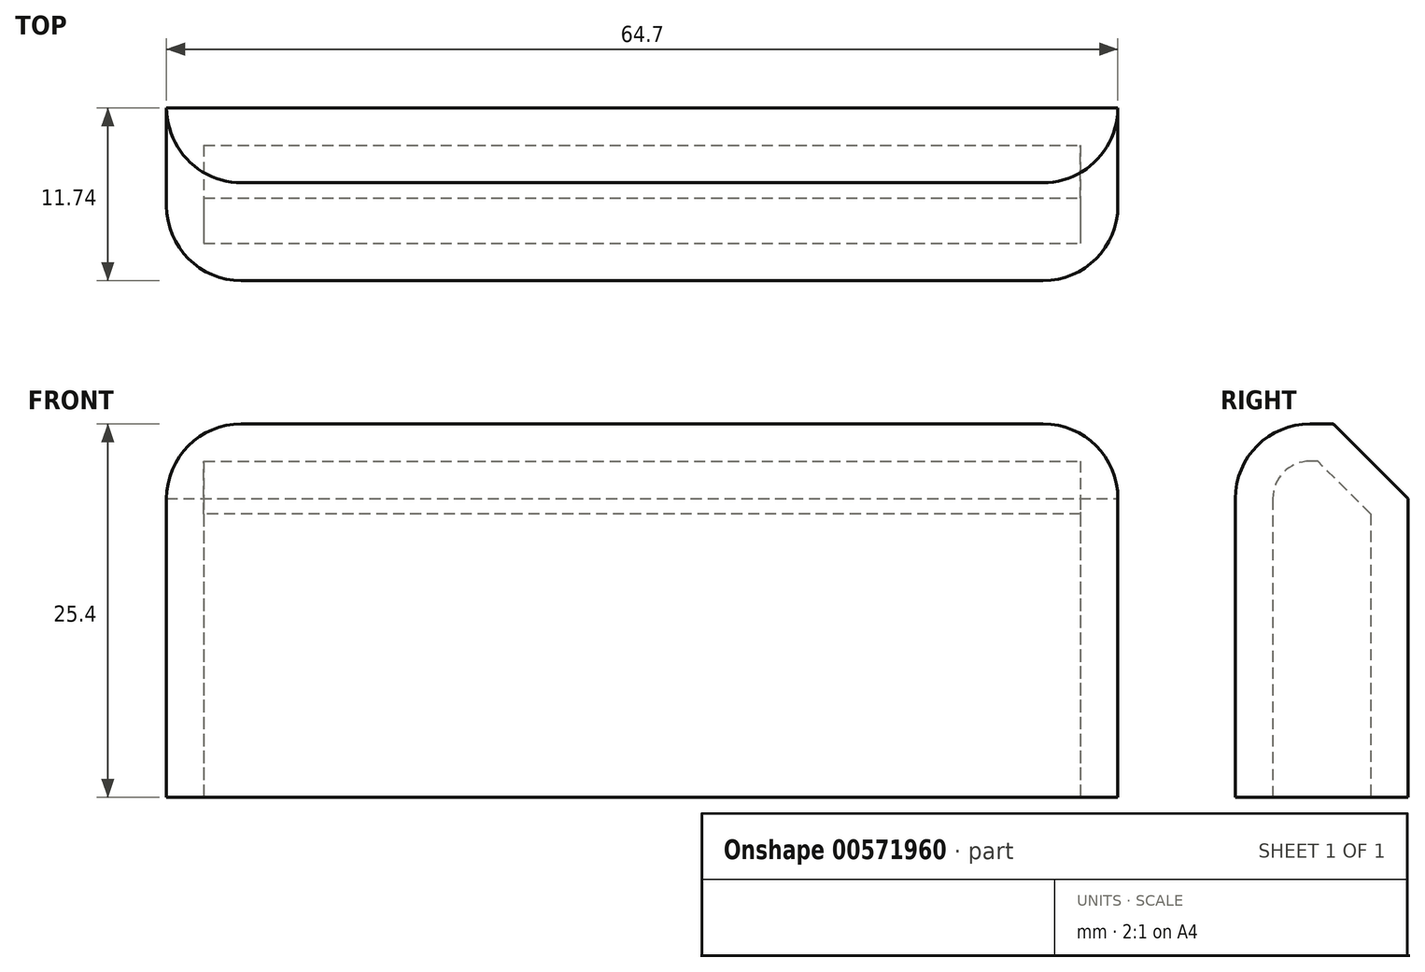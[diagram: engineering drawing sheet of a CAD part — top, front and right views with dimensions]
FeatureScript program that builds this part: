
annotation { "Feature Type Name" : "Feature", "Feature Type Description" : "" }
export const myFeature = defineFeature(function(context is Context, id is Id, definition is map)
    precondition{}
    {
        {
            var Q0;
            Q0=qCreatedBy(makeId("Top.planeOp"),FACE);
            var sketch = newSketch(context, id + "F0", { "sketchPlane" : qUnion([Q0])});
            skLineSegment(sketch, "E0.bottom", {"start": v(-24.66, 46.8) * mm, "end": v(40.04, 46.8) * mm});
            skLineSegment(sketch, "E0.top", {"start": v(-24.66, 35.06) * mm, "end": v(40.04, 35.06) * mm});
            skLineSegment(sketch, "E0.left", {"start": v(-24.66, 46.8) * mm, "end": v(-24.66, 35.06) * mm});
            skLineSegment(sketch, "E0.right", {"start": v(40.04, 46.8) * mm, "end": v(40.04, 35.06) * mm});
            skSolve(sketch);
        }
        {
            var Q0;
            Q0=makeQuery(id+"F0.imprint","IMPRINT",FACE,{"disambiguationData":[TD([[makeQuery(id+"F0.imprint","IMPRINT",EDGE,{"derivedFrom":sQuery(id+"F0.wireOp",EDGE,"E0.bottom")}),-1.0]])]});
            extrude(context, id + "F1", {"entities" : qUnion([Q0]), "depth" : 25.4 * mm, "offsetDistance" : 25.4 * mm});
        }
        {
            var Q0;
            Q0=makeQuery(id+"F1.opExtrude","CAP_EDGE",EDGE,{"disambiguationData":[OSD([sQuery(id+"F0.wireOp",EDGE,"E0.top")])],"isStart":false});
            fillet(context, id + "F2", {"entities" : qUnion([Q0]), "radius" : 5.08 * mm, "tangentPropagation" : true, "allowEdgeOverflow" : false});
        }
        {
            var Q0;
            Q0=makeQuery(id+"F1.opExtrude","CAP_EDGE",EDGE,{"disambiguationData":[OSD([sQuery(id+"F0.wireOp",EDGE,"E0.bottom")])],"isStart":false});
            chamfer(context, id + "F3", {"entities" : qUnion([Q0]), "width" : 5.08 * mm, "tangentPropagation" : true});
        }
        {
            var Q0;
            Q0=makeQuery(id+"F1.opExtrude","CAP_FACE",FACE,{"disambiguationData":[OSD([sQuery(id+"F0.wireOp",EDGE,"E0.bottom"),sQuery(id+"F0.wireOp",EDGE,"E0.top"),sQuery(id+"F0.wireOp",EDGE,"E0.left"),sQuery(id+"F0.wireOp",EDGE,"E0.right")])],"isStart":true});
            shell(context, id + "F4", {"entities" : qUnion([Q0]), "thickness" : 2.54 * mm});
        }
        {
            var Q0;
            Q0=makeQuery(id+"F1.opExtrude","SWEPT_EDGE",EDGE,{"disambiguationData":[OSD([sQuery(id+"F0.wireOp",EDGE,"E0.top"),sQuery(id+"F0.wireOp",EDGE,"E0.right")])]});
            var Q1;
            Q1=makeQuery(id+"F1.opExtrude","SWEPT_EDGE",EDGE,{"disambiguationData":[OSD([sQuery(id+"F0.wireOp",EDGE,"E0.top"),sQuery(id+"F0.wireOp",EDGE,"E0.left")])]});
            fillet(context, id + "F5", {"entities" : qUnion([Q0, Q1]), "radius" : 5.08 * mm, "tangentPropagation" : true, "allowEdgeOverflow" : false});
        }
    });
